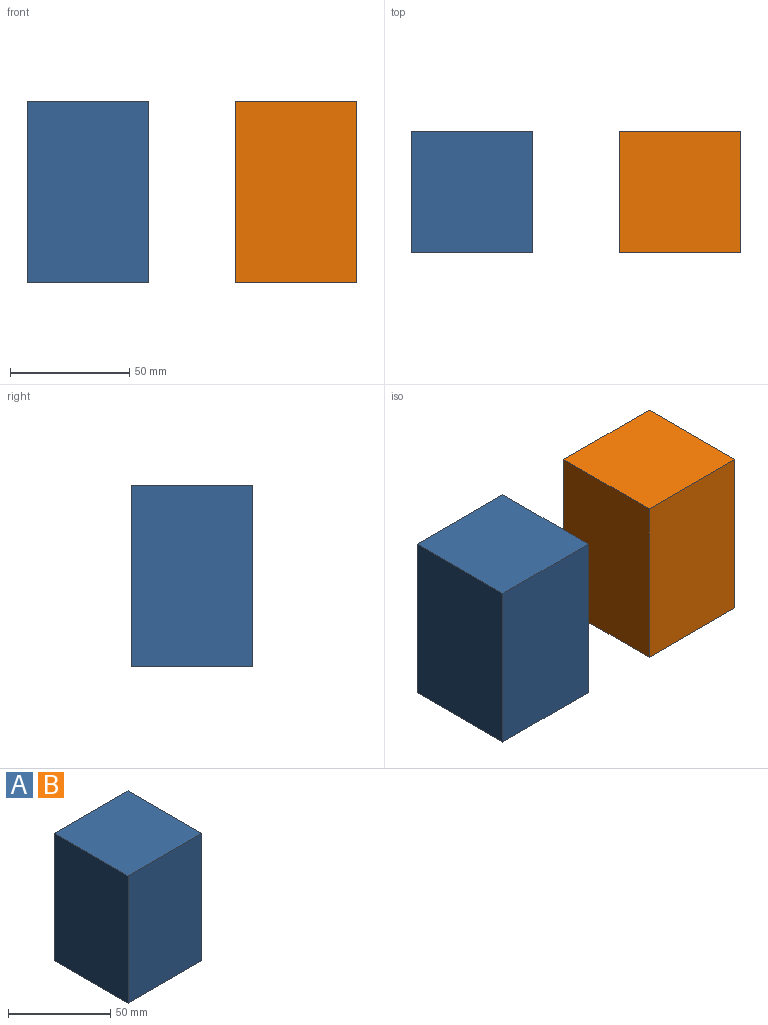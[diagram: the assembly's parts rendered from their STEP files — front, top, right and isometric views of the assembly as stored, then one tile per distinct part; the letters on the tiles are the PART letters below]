
ASSEMBLY  parts=2 mates=1
PART A: 23 faces, bbox 50.8x50.8x76.2 mm
  f0: plane 76.2x50.8mm, normal (-1,0,0), area 3871mm2, adj f1,f18,f20,f22
  f1: plane 50.8x50.8mm, normal (0,0,-1), area 604.8mm2, adj f0,f2,f16,f17,f19,f20,f21,f22
  f2: plane 73.03x44.45mm, normal (1,0,0), area 3246mm2, adj f1,f3,f19,f21
  f3: plane 44.45x6.35mm, normal (0,0,-1), area 282.3mm2, adj f2,f4,f19,f21
  f4: plane 50.8x44.45mm, normal (-1,0,0), area 2258.1mm2, adj f3,f5,f19,f21
  f5: plane 44.45x3.18mm, normal (0,0,-1), area 141.1mm2, adj f4,f6,f19,f21
  f6: plane 50.8x44.45mm, normal (1,0,0), area 2258.1mm2, adj f5,f7,f19,f21
  f7: plane 44.45x9.53mm, normal (0,0,-1), area 423.4mm2, adj f6,f8,f19,f21
  f8: plane 50.8x44.45mm, normal (-1,0,0), area 2258.1mm2, adj f7,f9,f19,f21
  f9: plane 44.45x3.18mm, normal (0,0,-1), area 141.1mm2, adj f8,f10,f19,f21
  f10: plane 50.8x44.45mm, normal (1,0,0), area 2258.1mm2, adj f9,f11,f19,f21
  f11: plane 44.45x9.53mm, normal (0,0,-1), area 423.4mm2, adj f10,f12,f19,f21
  f12: plane 50.8x44.45mm, normal (-1,0,0), area 2258.1mm2, adj f11,f13,f19,f21
  f13: plane 44.45x3.18mm, normal (0,0,-1), area 141.1mm2, adj f12,f14,f19,f21
  f14: plane 50.8x44.45mm, normal (1,0,0), area 2258.1mm2, adj f13,f15,f19,f21
  f15: plane 44.45x9.53mm, normal (0,0,-1), area 423.4mm2, adj f14,f16,f19,f21
  f16: plane 73.03x44.45mm, normal (-1,0,0), area 3246mm2, adj f1,f15,f19,f21
  f17: plane 76.2x50.8mm, normal (1,0,0), area 3871mm2, adj f1,f18,f20,f22
  f18: plane 50.8x50.8mm, normal (0,0,1), area 2580.6mm2, adj f0,f17,f20,f22
  f19: plane 73.03x44.45mm, normal (0,1,0), area 2762.1mm2, adj f1,f2,f3,f4,f5,f6,f7,f8
  f20: plane 76.2x50.8mm, normal (0,-1,0), area 3871mm2, adj f0,f1,f17,f18
  f21: plane 73.03x44.45mm, normal (0,-1,0), area 2762.1mm2, adj f1,f2,f3,f4,f5,f6,f7,f8
  f22: plane 76.2x50.8mm, normal (0,1,0), area 3871mm2, adj f0,f1,f17,f18
PART B: same geometry as A
PLACE A t=(33.91,5.39,44.13)mm
PLACE B t=(120.84,5.39,44.13)mm
MATE slider B.f0 <-> A.f17  axis (-1,0,0) through (95.44,5.39,34.6)mm
